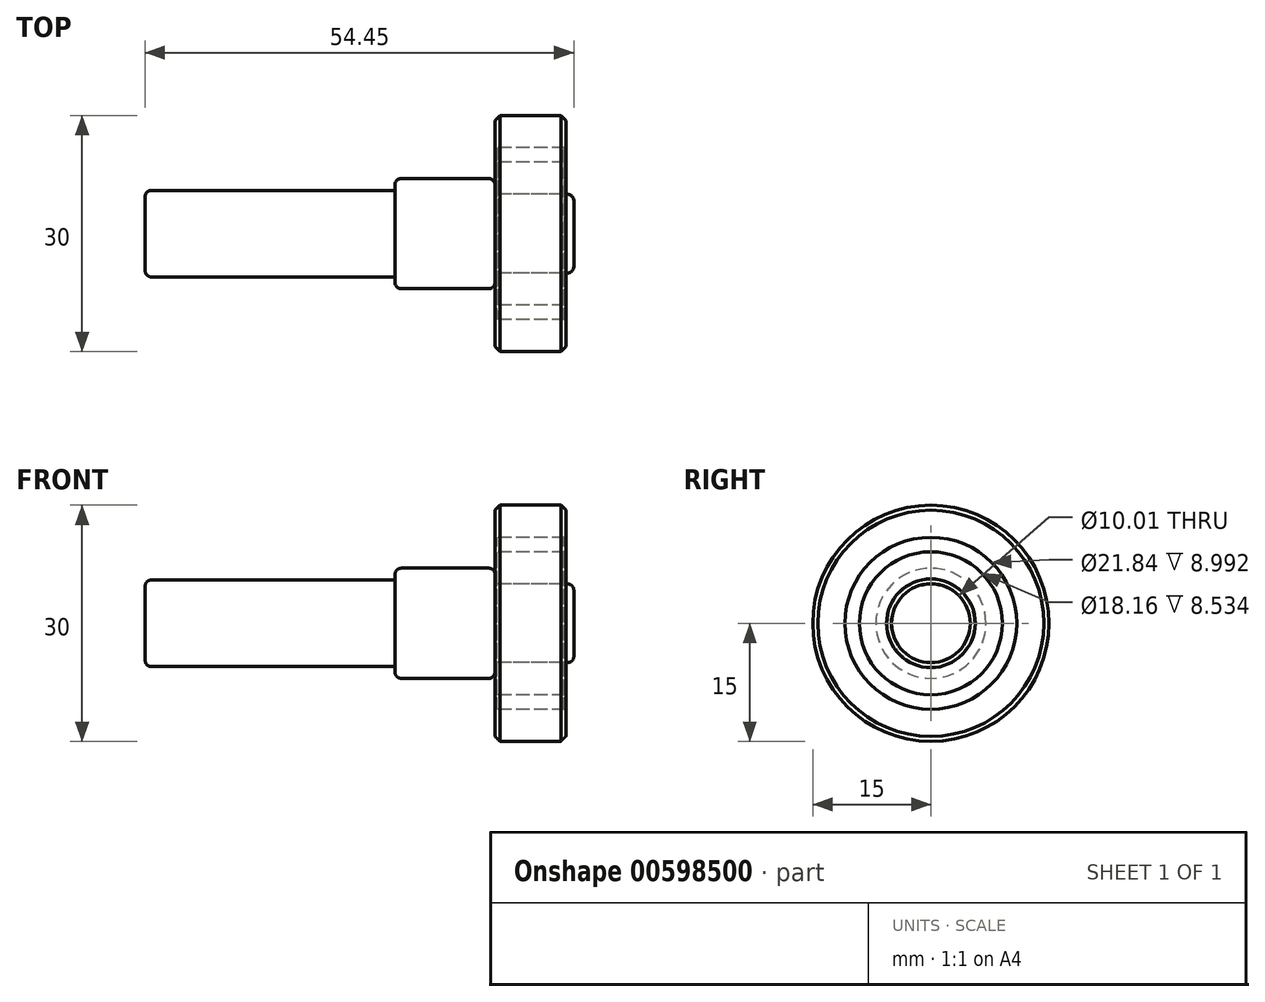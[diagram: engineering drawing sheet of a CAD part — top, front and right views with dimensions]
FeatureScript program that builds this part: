
annotation { "Feature Type Name" : "Feature", "Feature Type Description" : "" }
export const myFeature = defineFeature(function(context is Context, id is Id, definition is map)
    precondition{}
    {
        {
            var Q0;
            Q0=qCreatedBy(makeId("Right.planeOp"),FACE);
            var sketch = newSketch(context, id + "F0", { "sketchPlane" : qUnion([Q0])});
            skCircle(sketch, "E0", {"center": v(0, 0) * mm, "radius": 5 * mm});
            skSolve(sketch);
        }
        {
            var Q0;
            Q0 = qSketchRegion(id + "F0", true);
            extrude(context, id + "F1", {"entities" : qUnion([Q0]), "depth" : 10 * mm, "offsetDistance" : 25.4 * mm, "symmetric" : true});
        }
        {
            var Q0;
            Q0=makeQuery(id+"F1.opExtrude","CAP_FACE",FACE,{"disambiguationData":[OSD([sQuery(id+"F0.wireOp",EDGE,"E0")])],"isStart":true});
            var sketch = newSketch(context, id + "F2", { "sketchPlane" : qUnion([Q0])});
            skCircle(sketch, "E1", {"center": v(0, 0) * mm, "radius": 7 * mm});
            skSolve(sketch);
        }
        {
            var Q0;
            Q0=makeQuery(id+"F2.imprint","IMPRINT",FACE,{"disambiguationData":[TD([[makeQuery(id+"F2.imprint","IMPRINT",EDGE,{"derivedFrom":sQuery(id+"F2.wireOp",EDGE,"E1")}),1.0]])]});
            var Q1;
            Q1=makeQuery(id+"F2.imprint","IMPRINT",FACE,{"disambiguationData":[TD([[makeQuery(id+"F2.imprint","IMPRINT",EDGE,{"derivedFrom":makeQuery(id+"F1.opExtrude","CAP_EDGE",EDGE,{"disambiguationData":[OSD([sQuery(id+"F0.wireOp",EDGE,"E0")])],"isStart":true})}),-1.0]])]});
            extrude(context, id + "F3", {"entities" : qUnion([Q0, Q1]), "operationType" : NewBodyOperationType.ADD, "depth" : 12.7 * mm, "offsetDistance" : 25.4 * mm});
        }
        {
            var Q0;
            Q0=makeQuery(id+"F3.opExtrude","CAP_FACE",FACE,{"disambiguationData":[OSD([sQuery(id+"F2.wireOp",EDGE,"E1")])],"isStart":false});
            var sketch = newSketch(context, id + "F4", { "sketchPlane" : qUnion([Q0])});
            skCircle(sketch, "E2", {"center": v(0, 0) * mm, "radius": 5.5 * mm});
            skSolve(sketch);
        }
        {
            var Q0;
            Q0=makeQuery(id+"F4.imprint","IMPRINT",FACE,{"disambiguationData":[TD([[makeQuery(id+"F4.imprint","IMPRINT",EDGE,{"derivedFrom":sQuery(id+"F4.wireOp",EDGE,"E2")}),1.0]])]});
            extrude(context, id + "F5", {"entities" : qUnion([Q0]), "operationType" : NewBodyOperationType.ADD, "depth" : 31.75 * mm, "offsetDistance" : 25.4 * mm});
        }
        {
            var Q0;
            Q0=makeQuery(id+"F3.opExtrude","CAP_EDGE",EDGE,{"disambiguationData":[OSD([sQuery(id+"F2.wireOp",EDGE,"E1")])],"isStart":false});
            fillet(context, id + "F6", {"entities" : qUnion([Q0]), "radius" : 0.8 * mm, "tangentPropagation" : true, "allowEdgeOverflow" : false});
        }
        {
            var Q0;
            Q0=makeQuery(id+"F3.opExtrude","CAP_EDGE",EDGE,{"disambiguationData":[OSD([sQuery(id+"F2.wireOp",EDGE,"E1")])],"isStart":true});
            var Q1;
            Q1=makeQuery(id+"F1.opExtrude","CAP_EDGE",EDGE,{"disambiguationData":[OSD([sQuery(id+"F0.wireOp",EDGE,"E0")])],"isStart":false});
            fillet(context, id + "F7", {"entities" : qUnion([Q0, Q1]), "radius" : 0.8 * mm, "tangentPropagation" : true, "allowEdgeOverflow" : false});
        }
        {
            var Q0;
            Q0=makeQuery(id+"F5.opExtrude","CAP_EDGE",EDGE,{"disambiguationData":[OSD([sQuery(id+"F4.wireOp",EDGE,"E2")])],"isStart":false});
            fillet(context, id + "F8", {"entities" : qUnion([Q0]), "radius" : 0.8 * mm, "tangentPropagation" : true, "allowEdgeOverflow" : false});
        }
        {
            var Q0;
            Q0=makeQuery(id+"F3.opExtrude","CAP_FACE",FACE,{"disambiguationData":[OSD([sQuery(id+"F2.wireOp",EDGE,"E1")])],"isStart":true});
            var sketch = newSketch(context, id + "F9", { "sketchPlane" : qUnion([Q0])});
            skCircle(sketch, "E3", {"center": v(0, 0) * mm, "radius": 9.08 * mm});
            skCircle(sketch, "E4", {"center": v(0, 0) * mm, "radius": 10.92 * mm});
            skCircle(sketch, "E5", {"center": v(0, 0) * mm, "radius": 15 * mm});
            skCircle(sketch, "E6", {"center": v(0, 0) * mm, "radius": 5 * mm});
            skSolve(sketch);
        }
        {
            var Q0;
            Q0=makeQuery(id+"F9.imprint","IMPRINT",FACE,{"disambiguationData":[TD([[makeQuery(id+"F9.imprint","IMPRINT",EDGE,{"derivedFrom":sQuery(id+"F9.wireOp",EDGE,"E3")}),1.0]])]});
            var Q1;
            Q1=makeQuery(id+"F9.imprint","IMPRINT",FACE,{"disambiguationData":[TD([[makeQuery(id+"F9.imprint","IMPRINT",EDGE,{"derivedFrom":sQuery(id+"F9.wireOp",EDGE,"E4")}),-1.0]])]});
            var Q2;
            Q2=makeQuery(id+"F9.imprint","IMPRINT",FACE,{"disambiguationData":[TD([[makeQuery(id+"F9.imprint","IMPRINT",EDGE,{"derivedFrom":sQuery(id+"F9.wireOp",EDGE,"E6")}),-1.0]])]});
            extrude(context, id + "F10", {"entities" : qUnion([Q0, Q1, Q2]), "depth" : 9 * mm, "offsetDistance" : 25.4 * mm});
        }
        {
            var Q0;
            Q0=makeQuery(id+"F9.imprint","IMPRINT",FACE,{"disambiguationData":[TD([[makeQuery(id+"F9.imprint","IMPRINT",EDGE,{"derivedFrom":sQuery(id+"F9.wireOp",EDGE,"E3")}),-1.0]])]});
            extrude(context, id + "F11", {"entities" : qUnion([Q0]), "depth" : 8.76 * mm, "offsetDistance" : 25.4 * mm});
        }
        {
            var Q0;
            Q0=makeQuery(id+"F11.opExtrude","CAP_FACE",FACE,{"disambiguationData":[OSD([sQuery(id+"F9.wireOp",EDGE,"E3"),sQuery(id+"F9.wireOp",EDGE,"E4")])],"isStart":true});
            extrude(context, id + "F12", {"entities" : qUnion([Q0]), "operationType" : NewBodyOperationType.REMOVE, "oppositeDirection" : true, "depth" : 0.23 * mm, "offsetDistance" : 25.4 * mm});
        }
        {
            var Q0;
            Q0=makeQuery(id+"F10.opExtrude","CAP_EDGE",EDGE,{"disambiguationData":[OSD([sQuery(id+"F9.wireOp",EDGE,"E5")])],"isStart":false});
            var Q1;
            Q1=makeQuery(id+"F10.opExtrude","CAP_EDGE",EDGE,{"disambiguationData":[OSD([sQuery(id+"F9.wireOp",EDGE,"E5")])],"isStart":true});
            var Q2;
            Q2=makeQuery(id+"F7.opFillet","BLEND_FACE",FACE,{"disambiguationData":[OSD([sQuery(id+"F2.wireOp",EDGE,"E1")])]});
            var Q3;
            Q3=makeQuery(id+"F10.opExtrude","CAP_EDGE",EDGE,{"disambiguationData":[OSD([sQuery(id+"F9.wireOp",EDGE,"E6")])],"isStart":false});
            chamfer(context, id + "F13", {"entities" : qUnion([Q0, Q1, Q2, Q3]), "width" : 0.64 * mm, "tangentPropagation" : true});
        }
    });
